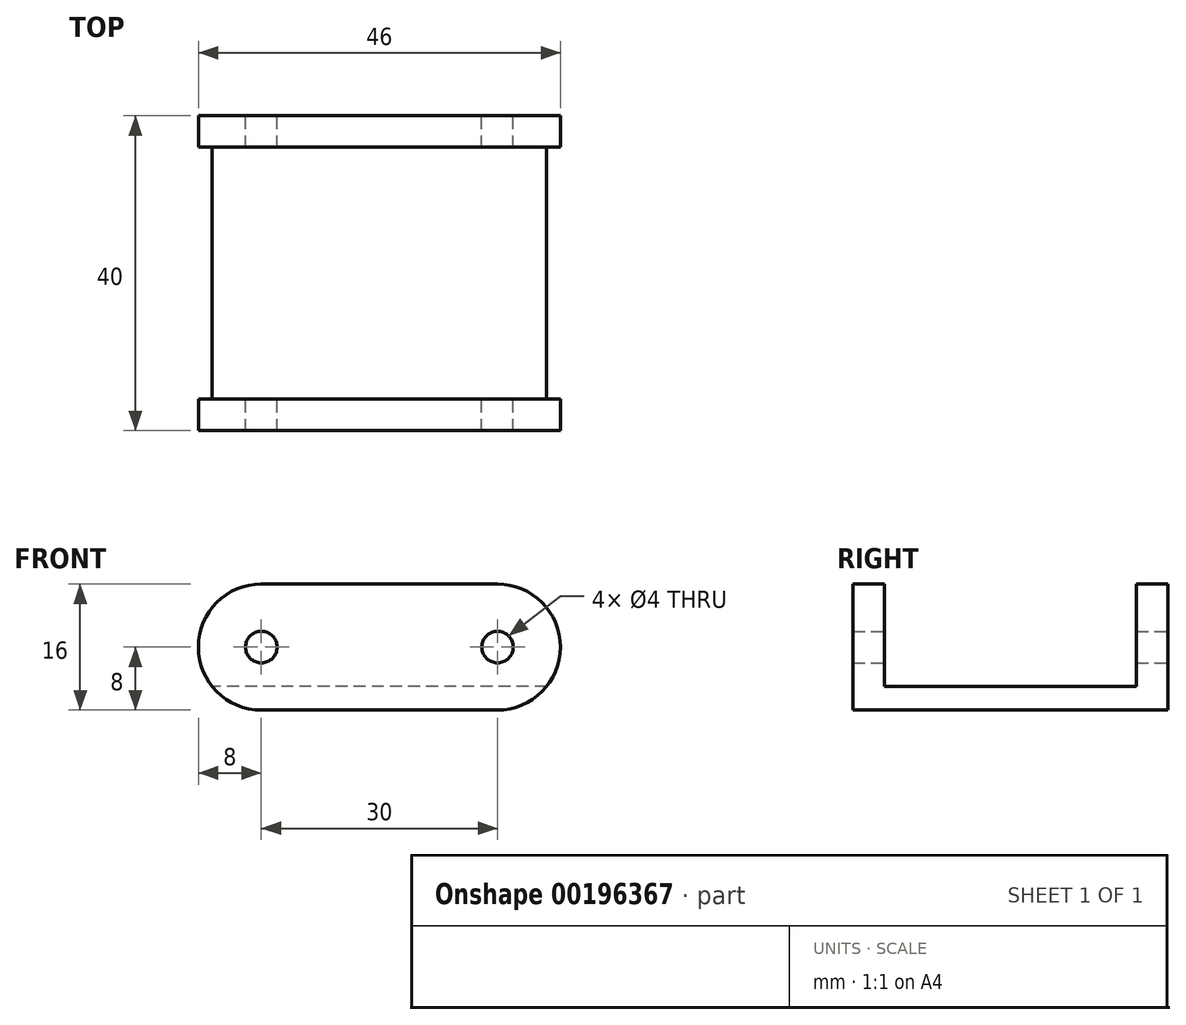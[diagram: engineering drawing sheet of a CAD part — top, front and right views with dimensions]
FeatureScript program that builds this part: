
annotation { "Feature Type Name" : "Feature", "Feature Type Description" : "" }
export const myFeature = defineFeature(function(context is Context, id is Id, definition is map)
    precondition{}
    {
        {
            var Q0;
            Q0=qCreatedBy(makeId("Front.planeOp"),FACE);
            var sketch = newSketch(context, id + "F0", { "sketchPlane" : qUnion([Q0])});
            skCircle(sketch, "E0", {"center": v(0, 0) * mm, "radius": 2 * mm});
            skCircle(sketch, "E1", {"center": v(30, 0) * mm, "radius": 2 * mm});
            skArc(sketch, "E2", {"start": v(0, 8) * mm, "mid": v(-8, 0) * mm, "end": v(0, -8) * mm});
            skArc(sketch, "E3", {"start": v(30, -8) * mm, "mid": v(38, 0) * mm, "end": v(30, 8) * mm});
            skLineSegment(sketch, "E4", {"start": v(0, -8) * mm, "end": v(30, -8) * mm});
            skLineSegment(sketch, "E5", {"start": v(0, 8) * mm, "end": v(30, 8) * mm});
            skSolve(sketch);
        }
        {
            var Q0;
            Q0=makeQuery(id+"F0.imprint","IMPRINT",FACE,{"disambiguationData":[TD([[makeQuery(id+"F0.imprint","IMPRINT",EDGE,{"derivedFrom":sQuery(id+"F0.wireOp",EDGE,"E0")}),-1.0]])]});
            extrude(context, id + "F1", {"entities" : qUnion([Q0]), "depth" : 40 * mm});
        }
        {
            var Q0;
            Q0=qCreatedBy(makeId("Right.planeOp"),FACE);
            var sketch = newSketch(context, id + "F2", { "sketchPlane" : qUnion([Q0])});
            skLineSegment(sketch, "E6", {"start": v(-36, 8) * mm, "end": v(-36, -5) * mm});
            skLineSegment(sketch, "E7", {"start": v(-36, -5) * mm, "end": v(-4, -5) * mm});
            skLineSegment(sketch, "E8", {"start": v(-4, -5) * mm, "end": v(-4, 8) * mm});
            skLineSegment(sketch, "E9", {"start": v(-4, 8) * mm, "end": v(-36, 8) * mm});
            skSolve(sketch);
        }
        {
            var Q0;
            Q0 = qSketchRegion(id + "F2", true);
            extrude(context, id + "F3", {"entities" : qUnion([Q0]), "operationType" : NewBodyOperationType.REMOVE, "endBound" : BoundingType.THROUGH_ALL, "depth" : 25 * mm, "hasSecondDirection" : true, "secondDirectionOppositeDirection" : true, "secondDirectionDepth" : 25 * mm});
        }
    });
